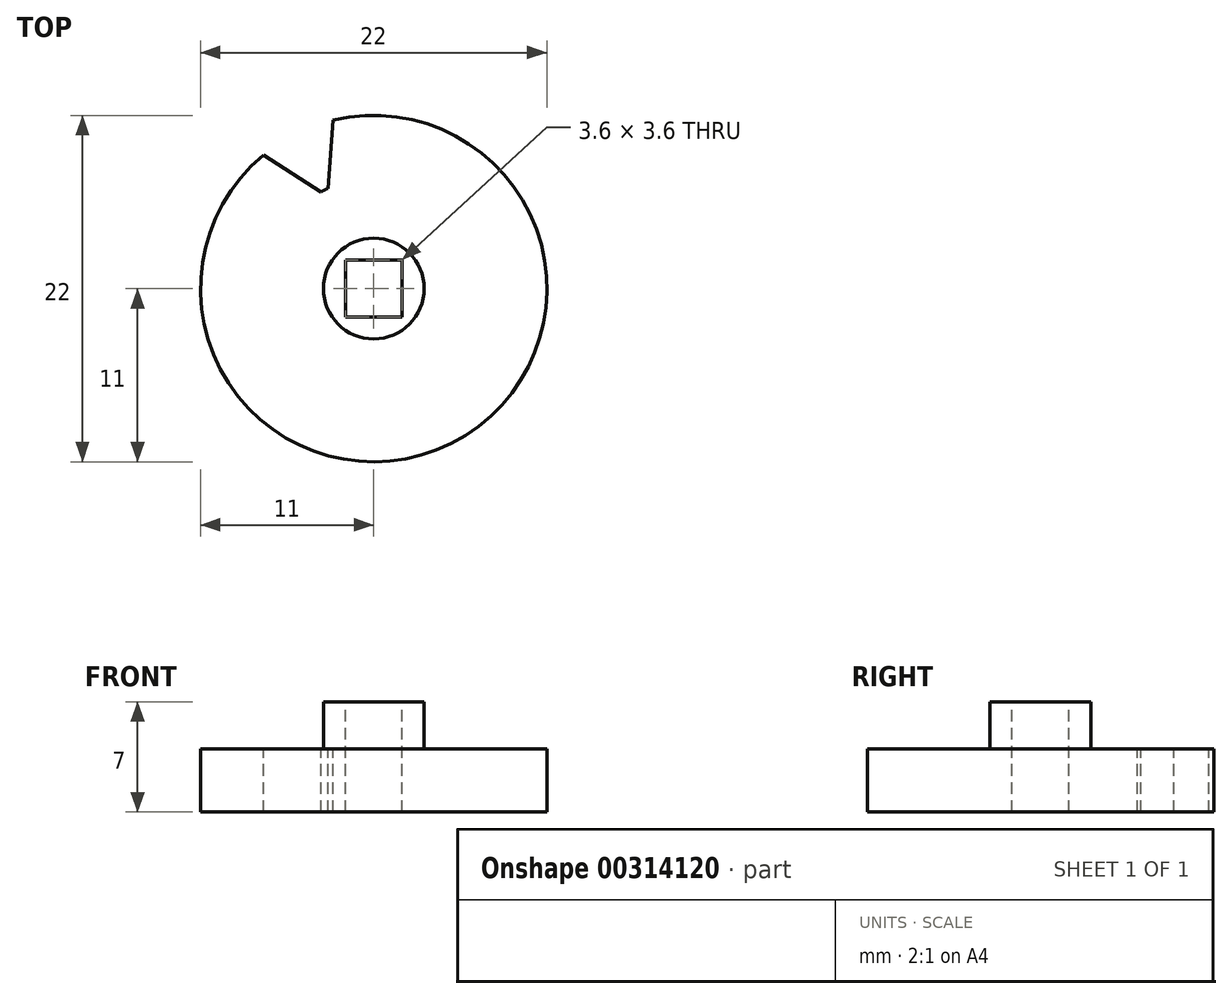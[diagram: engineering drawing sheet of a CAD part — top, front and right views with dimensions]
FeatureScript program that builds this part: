
annotation { "Feature Type Name" : "Feature", "Feature Type Description" : "" }
export const myFeature = defineFeature(function(context is Context, id is Id, definition is map)
    precondition{}
    {
        {
            var Q0;
            Q0=qCreatedBy(makeId("Top.planeOp"),FACE);
            var sketch = newSketch(context, id + "F0", { "sketchPlane" : qUnion([Q0])});
            skCircle(sketch, "E0", {"center": v(0, 0) * mm, "radius": 11 * mm});
            skSolve(sketch);
        }
        {
            var Q0;
            Q0=makeQuery(id+"F0.imprint","IMPRINT",FACE,{"disambiguationData":[TD([[makeQuery(id+"F0.imprint","IMPRINT",EDGE,{"derivedFrom":sQuery(id+"F0.wireOp",EDGE,"E0")}),1.0]])]});
            extrude(context, id + "F1", {"entities" : qUnion([Q0]), "depth" : 4 * mm});
        }
        {
            var Q0;
            Q0=makeQuery(id+"F1.opExtrude","CAP_FACE",FACE,{"disambiguationData":[OSD([sQuery(id+"F0.wireOp",EDGE,"E0")])],"isStart":false});
            var sketch = newSketch(context, id + "F2", { "sketchPlane" : qUnion([Q0])});
            skLineSegment(sketch, "E1", {"start": v(0, 0) * mm, "end": v(-4.92, 9.84) * mm});
            skLineSegment(sketch, "E2", {"start": v(0, 0) * mm, "end": v(-3.35, 6.15) * mm});
            skLineSegment(sketch, "E3.MirrorCS", {"start": v(0, 0) * mm, "end": v(-2.91, 6.37) * mm});
            skLineSegment(sketch, "E4", {"start": v(0, 0) * mm, "end": v(-7, 8.48) * mm});
            skLineSegment(sketch, "E5.MirrorCS", {"start": v(0, 0) * mm, "end": v(-2.58, 10.7) * mm});
            skArc(sketch, "E6", {"start": v(-3.35, 6.15) * mm, "mid": v(-3.13, 6.26) * mm, "end": v(-2.91, 6.37) * mm});
            skLineSegment(sketch, "E7", {"start": v(-7, 8.48) * mm, "end": v(-3.35, 6.15) * mm});
            skLineSegment(sketch, "E8", {"start": v(-2.58, 10.7) * mm, "end": v(-2.91, 6.37) * mm});
            skArc(sketch, "E9", {"start": v(-7, 8.48) * mm, "mid": v(-4.92, 9.84) * mm, "end": v(-2.58, 10.7) * mm});
            skSolve(sketch);
        }
        {
            var Q0;
            {var subQ5=sQuery(id+"F2.wireOp",EDGE,"E7");Q0=makeQuery(id+"F2.imprint","IMPRINT",FACE,{"disambiguationData":[TD([[makeQuery(id+"F2.imprint","IMPRINT",EDGE,{"derivedFrom":subQ5}),1.0]])]});}
            var Q1;
            {var subQ5=sQuery(id+"F2.wireOp",EDGE,"E8");Q1=makeQuery(id+"F2.imprint","IMPRINT",FACE,{"disambiguationData":[TD([[makeQuery(id+"F2.imprint","IMPRINT",EDGE,{"derivedFrom":subQ5}),-1.0]])]});}
            extrude(context, id + "F3", {"entities" : qUnion([Q0, Q1]), "operationType" : NewBodyOperationType.REMOVE, "endBound" : BoundingType.THROUGH_ALL, "oppositeDirection" : true, "depth" : 25 * mm});
        }
        {
            var Q0;
            Q0=qCreatedBy(makeId("Front.planeOp"),FACE);
            var sketch = newSketch(context, id + "F4", { "sketchPlane" : qUnion([Q0])});
            skLineSegment(sketch, "E10", {"start": v(0, 0) * mm, "end": v(0, -5.62) * mm});
            skSolve(sketch);
        }
        {
            var Q0;
            Q0=makeQuery(id+"F1.opExtrude","CAP_FACE",FACE,{"disambiguationData":[OSD([sQuery(id+"F0.wireOp",EDGE,"E0")])],"isStart":false});
            var sketch = newSketch(context, id + "F5", { "sketchPlane" : qUnion([Q0])});
            skCircle(sketch, "E11", {"center": v(0, 0) * mm, "radius": 3.2 * mm});
            skSolve(sketch);
        }
        {
            var Q0;
            Q0 = qSketchRegion(id + "F5", true);
            extrude(context, id + "F6", {"entities" : qUnion([Q0]), "operationType" : NewBodyOperationType.ADD, "depth" : 3 * mm});
        }
        {
            var Q0;
            Q0=makeQuery(id+"F6.opExtrude","CAP_FACE",FACE,{"disambiguationData":[OSD([sQuery(id+"F5.wireOp",EDGE,"E11")])],"isStart":false});
            var sketch = newSketch(context, id + "F7", { "sketchPlane" : qUnion([Q0])});
            skLineSegment(sketch, "E12.bottom", {"start": v(1.8, 1.8) * mm, "end": v(-1.8, 1.8) * mm});
            skLineSegment(sketch, "E12.top", {"start": v(1.8, -1.8) * mm, "end": v(-1.8, -1.8) * mm});
            skLineSegment(sketch, "E12.left", {"start": v(1.8, 1.8) * mm, "end": v(1.8, -1.8) * mm});
            skLineSegment(sketch, "E12.right", {"start": v(-1.8, 1.8) * mm, "end": v(-1.8, -1.8) * mm});
            skPoint(sketch, "E12.middle", {"position": v(0, 0) * mm});
            skSolve(sketch);
        }
        {
            var Q0;
            Q0 = qSketchRegion(id + "F7", true);
            extrude(context, id + "F8", {"entities" : qUnion([Q0]), "operationType" : NewBodyOperationType.REMOVE, "endBound" : BoundingType.THROUGH_ALL, "oppositeDirection" : true, "depth" : 25 * mm});
        }
    });
